# Revit family: Power-ModularDevices-GEWISS-90AM-BUZZER
name_source: partatom
category: Apparecchi elettrici
revit_build: Autodesk Revit 2016 (Build: 20161004_0715(x64)
units: mm (PartAtom-declared; Revit-internal decimal feet)

## family parameters
Condiviso = No
Host = Superficie
Mantenere orientamento annotazione = Sì
Numero OmniClass = 23.80.50.00
Punto di calcolo locali = Sì
Quota connettore circolare = Usa diametro
Taglio con vuoti quando caricato = No
Tipo di parte = Normale
Titolo OmniClass = Terminals for Power Supply

## types (2) — shared parameters
Catalogue = POWER
Catalogue Range = 90 AM
Electrocod = 140
IDF = a591a86b-9862-4f47-9229-274487fbb6be
IDT = c61a7052-8553-4e3b-a73d-0af44cd32236
Immagine tipo = GW96406.jpg
No. Chorus modules = 1
No. of modules EN 50022 = 1
Numero di poli = 1
Produttore = GEWISS S.p.A.
Prospetto di default = 1219 mm
SEO = Buzzer
Technical sheet = https://www.gewiss.com
URL = https://www.gewiss.com
Version file RFA = 18.0
carico = Altro
potenza in watt = 0 V

## per-type parameters (varying)
| type | Descrizione | EAN code | Modello | Power loss | Rated voltage |
| GW96407 - BUZZER 230V AC 1M. | BUZZER 230V AC 1M. | 8011564063679 | GW96407 | 10VA | 230V |
| GW96406 - BUZZER 12V AC 1M. | BUZZER 12V AC 1M. | 8011564063662 | GW96406 | 5VA | 12V |
